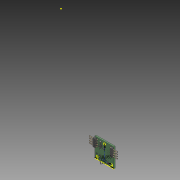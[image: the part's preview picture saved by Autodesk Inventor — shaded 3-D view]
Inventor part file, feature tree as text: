
AUTODESK INVENTOR PART (.ipt)
format: ipt  version: 2020 (Build 240168000, 168)  size: 603,136 bytes
history: native  units: in
note: dims shown in document units (in); Inventor stores cm internally (conversion verified against a paired STEP export)
features: other x12, sketch x1
ambient origin geometry x8: Origin, YZ Plane, XZ Plane, XY Plane, X Axis, Y Axis, Z Axis, Center Point
bodies: Solid1 (feature_tree)
feature tree (13):
  other  "SmallEncoder.iam"
  other  "C_0603_1608Metric.iam:1::SOLID_1.ipt:1"
  other  "C_0603_1608Metric.iam:2::SOLID_1.ipt:1"
  other  "C_0603_1608Metric.iam:3::SOLID_1.ipt:1"
  other  "R_0603_1608Metric.iam:1::SOLID_2.ipt:1"
  other  "R_0603_1608Metric.iam:2::SOLID_2.ipt:1"
  other  "C_0603_1608Metric.iam:4::SOLID_1.ipt:1"
  other  "C_0805_2012Metric.iam:1::SOLID_3.ipt:1"
  other  "PinHeader_1x04_P2.54mm_Horizontal.iam:1::SOLID_4.ipt:1"
  other  "PinHeader_1x04_P2.54mm_Horizontal.iam:2::SOLID_4.ipt:1"
  other  "SOT-23-5.iam:1::SOLID_5.ipt:1"
  other  "COMPOUND.ipt:1"
  sketch  "Sketch1"  dims[d0=0.3937in d1=0.7461in d2=0.748in d3=0.9843in]
